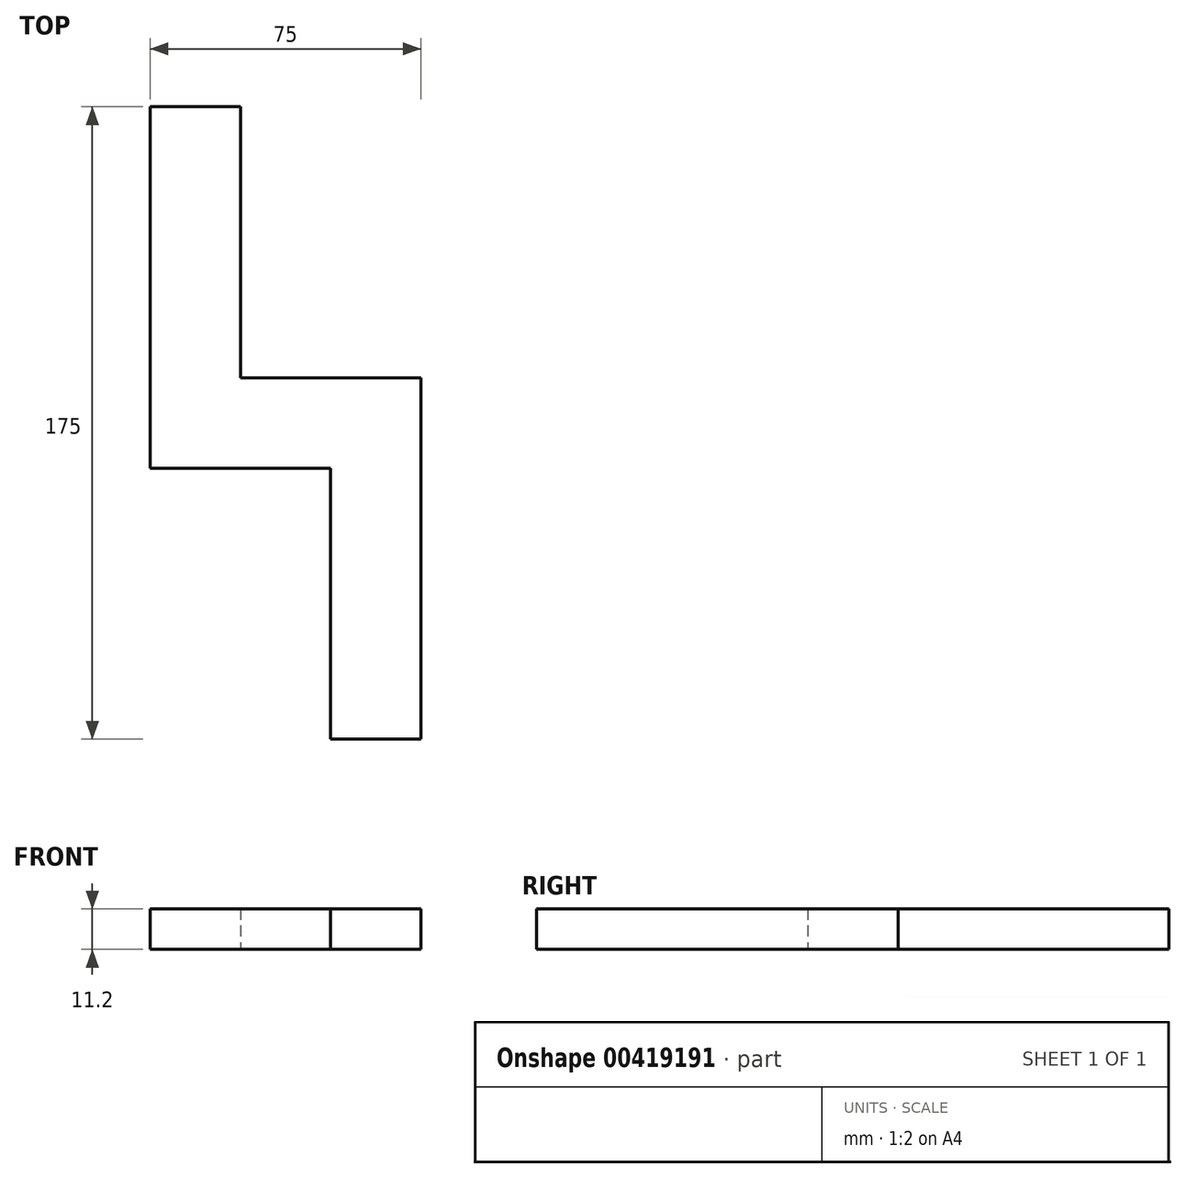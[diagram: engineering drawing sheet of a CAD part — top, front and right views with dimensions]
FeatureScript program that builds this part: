
annotation { "Feature Type Name" : "Feature", "Feature Type Description" : "" }
export const myFeature = defineFeature(function(context is Context, id is Id, definition is map)
    precondition{}
    {
        {
            var Q0;
            Q0=qCreatedBy(makeId("Top.planeOp"),FACE);
            var sketch = newSketch(context, id + "F0", { "sketchPlane" : qUnion([Q0])});
            skLineSegment(sketch, "E0.bottom", {"start": v(-36.28, 103.4) * mm, "end": v(-11.28, 103.4) * mm});
            skLineSegment(sketch, "E0.top", {"start": v(-36.28, 28.4) * mm, "end": v(-11.28, 28.4) * mm});
            skLineSegment(sketch, "E0.left", {"start": v(-36.28, 103.4) * mm, "end": v(-36.28, 28.4) * mm});
            skLineSegment(sketch, "E0.right", {"start": v(-11.28, 103.4) * mm, "end": v(-11.28, 28.4) * mm});
            skLineSegment(sketch, "E1.bottom", {"start": v(-36.28, 28.4) * mm, "end": v(38.72, 28.4) * mm});
            skLineSegment(sketch, "E1.top", {"start": v(-36.28, 3.4) * mm, "end": v(38.72, 3.4) * mm});
            skLineSegment(sketch, "E1.left", {"start": v(-36.28, 28.4) * mm, "end": v(-36.28, 3.4) * mm});
            skLineSegment(sketch, "E1.right", {"start": v(38.72, 28.4) * mm, "end": v(38.72, 3.4) * mm});
            skLineSegment(sketch, "E2.bottom", {"start": v(38.72, 3.4) * mm, "end": v(13.72, 3.4) * mm});
            skLineSegment(sketch, "E2.top", {"start": v(38.72, -71.6) * mm, "end": v(13.72, -71.6) * mm});
            skLineSegment(sketch, "E2.left", {"start": v(38.72, 3.4) * mm, "end": v(38.72, -71.6) * mm});
            skLineSegment(sketch, "E2.right", {"start": v(13.72, 3.4) * mm, "end": v(13.72, -71.6) * mm});
            skSolve(sketch);
        }
        {
            var Q0;
            Q0 = qSketchRegion(id + "F0", true);
            extrude(context, id + "F1", {"entities" : qUnion([Q0]), "depth" : 11.2 * mm});
        }
    });
